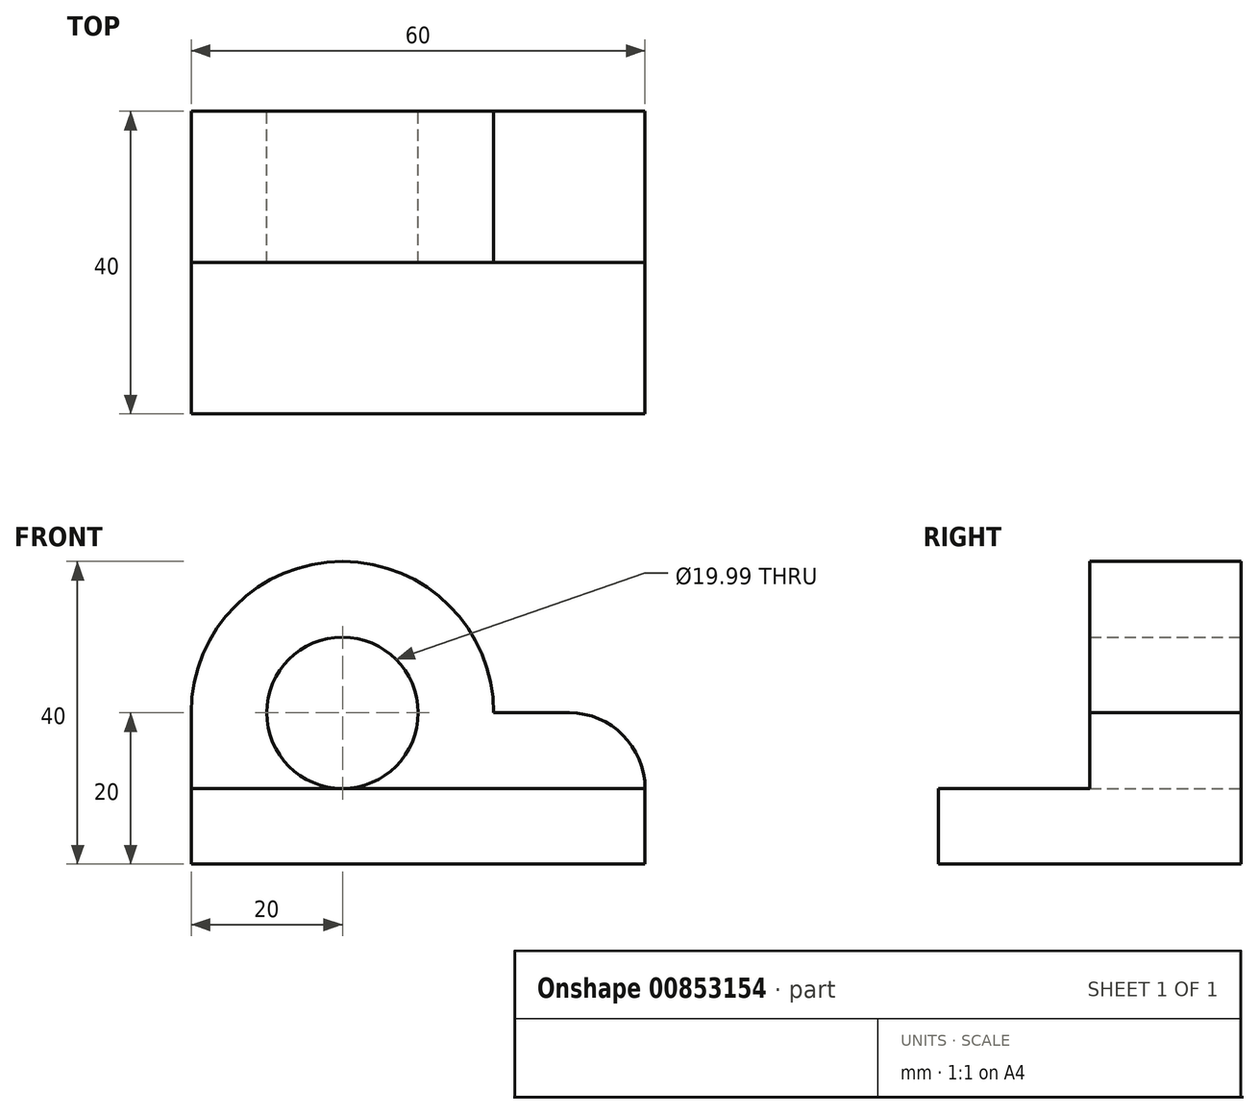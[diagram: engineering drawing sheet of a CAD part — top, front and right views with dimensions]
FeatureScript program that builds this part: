
annotation { "Feature Type Name" : "Feature", "Feature Type Description" : "" }
export const myFeature = defineFeature(function(context is Context, id is Id, definition is map)
    precondition{}
    {
        {
            var Q0;
            Q0=qCreatedBy(makeId("Front.planeOp"),FACE);
            var sketch = newSketch(context, id + "F0", { "sketchPlane" : qUnion([Q0])});
            skLineSegment(sketch, "E0.bottom", {"start": v(0, 0) * mm, "end": v(60, 0) * mm});
            skLineSegment(sketch, "E0.top", {"start": v(0, 10) * mm, "end": v(60, 10) * mm});
            skLineSegment(sketch, "E0.left", {"start": v(0, 0) * mm, "end": v(0, 10) * mm});
            skLineSegment(sketch, "E0.right", {"start": v(60, 0) * mm, "end": v(60, 10) * mm});
            skLineSegment(sketch, "E1", {"start": v(60, 10) * mm, "end": v(60, 10) * mm});
            skLineSegment(sketch, "E2", {"start": v(0, 10) * mm, "end": v(0, 20) * mm});
            skLineSegment(sketch, "E3", {"start": v(0, 20) * mm, "end": v(50, 20) * mm});
            skLineSegment(sketch, "E4", {"start": v(0, 20) * mm, "end": v(20, 20) * mm});
            skCircle(sketch, "E5", {"center": v(20, 20) * mm, "radius": 10 * mm});
            skPoint(sketch, "E6.visualSharp", {"position": v(60, 20) * mm});
            skArc(sketch, "E6.filletArc", {"start": v(60, 10) * mm, "mid": v(57.07, 17.07) * mm, "end": v(50, 20) * mm});
            skArc(sketch, "E7.trimOffspring", {"start": v(40, 20) * mm, "mid": v(20, 40) * mm, "end": v(0, 20) * mm});
            skSolve(sketch);
        }
        {
            var Q0;
            Q0=makeQuery(id+"F0.imprint","IMPRINT",FACE,{"disambiguationData":[TD([[makeQuery(id+"F0.imprint","IMPRINT",EDGE,{"derivedFrom":sQuery(id+"F0.wireOp",EDGE,"E0.bottom")}),1.0]])]});
            extrude(context, id + "F1", {"entities" : qUnion([Q0]), "depth" : 40 * mm, "offsetDistance" : 25 * mm});
        }
        {
            var Q0;
            {var subQ0=sQuery(id+"F0.wireOp",EDGE,"E7.trimOffspring");Q0=makeQuery(id+"F0.imprint","IMPRINT",FACE,{"disambiguationData":[TD([[makeQuery(id+"F0.imprint","IMPRINT",EDGE,{"derivedFrom":subQ0}),1.0]])]});}
            var Q1;
            Q1=makeQuery(id+"F0.imprint","IMPRINT",FACE,{"disambiguationData":[TD([[makeQuery(id+"F0.imprint","IMPRINT",EDGE,{"derivedFrom":sQuery(id+"F0.wireOp",EDGE,"E0.top")}),1.0]])]});
            extrude(context, id + "F2", {"entities" : qUnion([Q0, Q1]), "operationType" : NewBodyOperationType.ADD, "depth" : 20 * mm, "offsetDistance" : 25 * mm});
        }
    });
